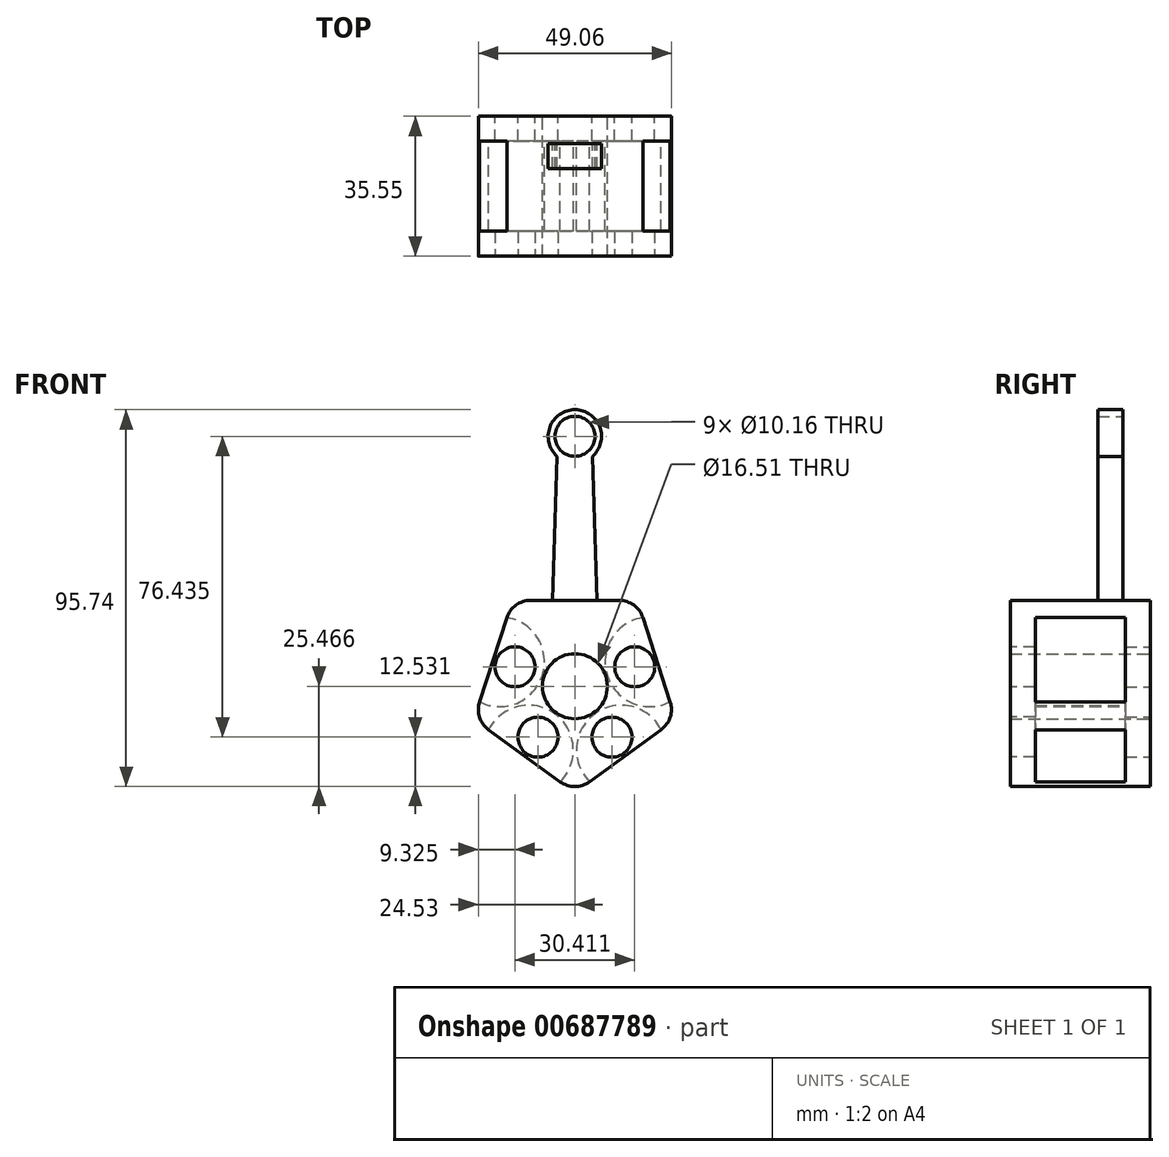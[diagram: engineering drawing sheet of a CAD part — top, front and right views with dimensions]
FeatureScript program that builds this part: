
annotation { "Feature Type Name" : "Feature", "Feature Type Description" : "" }
export const myFeature = defineFeature(function(context is Context, id is Id, definition is map)
    precondition{}
    {
        {
            var Q0;
            Q0=qCreatedBy(makeId("Front.planeOp"),FACE);
            var sketch = newSketch(context, id + "F0", { "sketchPlane" : qUnion([Q0])});
            skPoint(sketch, "E0", {"position": v(-16.39, -3.78) * mm});
            skCircle(sketch, "E1", {"center": v(-16.39, -3.78) * mm, "radius": 8.26 * mm});
            skLineSegment(sketch, "E2.0", {"start": v(-27.63, 18.03) * mm, "end": v(-5.15, 18.03) * mm});
            skLineSegment(sketch, "E2.1", {"start": v(0.89, 13.64) * mm, "end": v(7.83, -7.73) * mm});
            skLineSegment(sketch, "E2.2", {"start": v(5.52, -14.83) * mm, "end": v(-12.66, -28.04) * mm});
            skLineSegment(sketch, "E2.3", {"start": v(-20.12, -28.04) * mm, "end": v(-38.3, -14.83) * mm});
            skLineSegment(sketch, "E2.4", {"start": v(-40.61, -7.73) * mm, "end": v(-33.67, 13.64) * mm});
            skPoint(sketch, "E3", {"position": v(-37.14, 2.96) * mm});
            skPoint(sketch, "E4", {"position": v(-26.76, -0.41) * mm});
            skPoint(sketch, "E5", {"position": v(-31.6, 1.16) * mm});
            skCircle(sketch, "E6", {"center": v(-31.6, 1.16) * mm, "radius": 5.08 * mm});
            skPoint(sketch, "E7", {"position": v(-16.39, 7.12) * mm});
            skPoint(sketch, "E8", {"position": v(4.36, 2.96) * mm});
            skPoint(sketch, "E9", {"position": v(-6.02, -0.41) * mm});
            skPoint(sketch, "E10", {"position": v(-3.57, -21.43) * mm});
            skPoint(sketch, "E11", {"position": v(-29.21, -21.43) * mm});
            skPoint(sketch, "E12", {"position": v(-9.98, -12.6) * mm});
            skPoint(sketch, "E13", {"position": v(-22.8, -12.6) * mm});
            skPoint(sketch, "E14", {"position": v(-1.18, 1.16) * mm});
            skPoint(sketch, "E15", {"position": v(-7, -16.72) * mm});
            skPoint(sketch, "E16", {"position": v(-25.79, -16.72) * mm});
            skCircle(sketch, "E17", {"center": v(-1.18, 1.16) * mm, "radius": 5.08 * mm});
            skCircle(sketch, "E18", {"center": v(-7, -16.72) * mm, "radius": 5.08 * mm});
            skCircle(sketch, "E19", {"center": v(-25.79, -16.72) * mm, "radius": 5.08 * mm});
            skPoint(sketch, "E20.orphan", {"position": v(-36.43, 2.73) * mm});
            skPoint(sketch, "E21.orphan", {"position": v(3.65, 2.73) * mm});
            skPoint(sketch, "E22.end.orphan", {"position": v(-4, -20.83) * mm});
            skPoint(sketch, "E23.end.orphan", {"position": v(-28.77, -20.83) * mm});
            skPoint(sketch, "E24", {"position": v(-24.32, 18.03) * mm});
            skPoint(sketch, "E25", {"position": v(-8.46, 18.03) * mm});
            skPoint(sketch, "E26.visualSharp", {"position": v(-32.24, 18.03) * mm});
            skArc(sketch, "E26.filletArc", {"start": v(-27.63, 18.03) * mm, "mid": v(-31.36, 16.82) * mm, "end": v(-33.67, 13.64) * mm});
            skPoint(sketch, "E27.visualSharp", {"position": v(-0.54, 18.03) * mm});
            skArc(sketch, "E27.filletArc", {"start": v(0.89, 13.64) * mm, "mid": v(-1.42, 16.82) * mm, "end": v(-5.15, 18.03) * mm});
            skPoint(sketch, "E28.visualSharp", {"position": v(9.26, -12.12) * mm});
            skArc(sketch, "E28.filletArc", {"start": v(5.52, -14.83) * mm, "mid": v(7.83, -11.65) * mm, "end": v(7.83, -7.73) * mm});
            skPoint(sketch, "E29.visualSharp", {"position": v(-16.39, -30.75) * mm});
            skArc(sketch, "E29.filletArc", {"start": v(-20.12, -28.04) * mm, "mid": v(-16.39, -29.25) * mm, "end": v(-12.66, -28.04) * mm});
            skPoint(sketch, "E30.visualSharp", {"position": v(-42.04, -12.12) * mm});
            skArc(sketch, "E30.filletArc", {"start": v(-40.61, -7.73) * mm, "mid": v(-40.61, -11.65) * mm, "end": v(-38.3, -14.83) * mm});
            skSolve(sketch);
        }
        {
            var Q0;
            Q0=makeQuery(id+"F0.imprint","IMPRINT",FACE,{"disambiguationData":[TD([[makeQuery(id+"F0.imprint","IMPRINT",EDGE,{"derivedFrom":sQuery(id+"F0.wireOp",EDGE,"E1")}),-1.0]])]});
            extrude(context, id + "F1", {"entities" : qUnion([Q0]), "depth" : 6.35 * mm, "offsetDistance" : 25.4 * mm});
        }
        {
            var Q0;
            Q0=makeQuery(id+"F1.opExtrude","CAP_FACE",FACE,{"disambiguationData":[OSD([sQuery(id+"F0.wireOp",EDGE,"E1"),sQuery(id+"F0.wireOp",EDGE,"E2.0"),sQuery(id+"F0.wireOp",EDGE,"E2.1"),sQuery(id+"F0.wireOp",EDGE,"E2.2"),sQuery(id+"F0.wireOp",EDGE,"E2.3"),sQuery(id+"F0.wireOp",EDGE,"E2.4"),sQuery(id+"F0.wireOp",EDGE,"E6"),sQuery(id+"F0.wireOp",EDGE,"E17"),sQuery(id+"F0.wireOp",EDGE,"E18"),sQuery(id+"F0.wireOp",EDGE,"E19"),sQuery(id+"F0.wireOp",EDGE,"E26.filletArc"),sQuery(id+"F0.wireOp",EDGE,"E27.filletArc"),sQuery(id+"F0.wireOp",EDGE,"E28.filletArc"),sQuery(id+"F0.wireOp",EDGE,"E29.filletArc"),sQuery(id+"F0.wireOp",EDGE,"E30.filletArc")])],"isStart":false});
            var sketch = newSketch(context, id + "F2", { "sketchPlane" : qUnion([Q0])});
            skArc(sketch, "E31", {"start": v(-40.61, -7.73) * mm, "mid": v(-24.66, -1.1) * mm, "end": v(-33.67, 13.64) * mm});
            skArc(sketch, "E32", {"start": v(0.89, 13.64) * mm, "mid": v(-8.15, -1.1) * mm, "end": v(7.83, -7.73) * mm});
            skArc(sketch, "E33", {"start": v(5.52, -14.83) * mm, "mid": v(-11.3, -10.8) * mm, "end": v(-12.66, -28.04) * mm});
            skArc(sketch, "E34", {"start": v(-20.12, -28.04) * mm, "mid": v(-21.48, -10.8) * mm, "end": v(-38.3, -14.83) * mm});
            skSolve(sketch);
        }
        {
            var Q0;
            Q0 = qSketchRegion(id + "F2", true);
            var Q1;
            Q1=makeQuery(id+"F2.imprint","IMPRINT",FACE,{"disambiguationData":[TD([[makeQuery(id+"F2.imprint","IMPRINT",EDGE,{"derivedFrom":sQuery(id+"F2.wireOp",EDGE,"E31")}),-1.0]])]});
            extrude(context, id + "F3", {"entities" : qUnion([Q0, Q1]), "operationType" : NewBodyOperationType.ADD, "depth" : (.75 - (.25 / 2)) * mm, "offsetDistance" : 25.4 * mm});
        }
        {
            var Q0;
            Q0=makeQuery(id+"F3.opExtrude","CAP_FACE",FACE,{"disambiguationData":[OSD([sQuery(id+"F0.wireOp",EDGE,"E1"),sQuery(id+"F0.wireOp",EDGE,"E2.0"),sQuery(id+"F0.wireOp",EDGE,"E26.filletArc"),sQuery(id+"F0.wireOp",EDGE,"E27.filletArc"),sQuery(id+"F0.wireOp",EDGE,"E28.filletArc"),sQuery(id+"F0.wireOp",EDGE,"E29.filletArc"),sQuery(id+"F0.wireOp",EDGE,"E30.filletArc"),sQuery(id+"F2.wireOp",EDGE,"E31"),sQuery(id+"F2.wireOp",EDGE,"E32"),sQuery(id+"F2.wireOp",EDGE,"E33"),sQuery(id+"F2.wireOp",EDGE,"E34")])],"isStart":false});
            var sketch = newSketch(context, id + "F4", { "sketchPlane" : qUnion([Q0])});
            skPoint(sketch, "E35", {"position": v(-16.39, -3.78) * mm});
            skPoint(sketch, "E36", {"position": v(-16.39, 59.72) * mm});
            skCircle(sketch, "E37", {"center": v(-16.39, 59.72) * mm, "radius": 5.08 * mm});
            skCircle(sketch, "E38", {"center": v(-16.39, 59.72) * mm, "radius": 6.77 * mm});
            skPoint(sketch, "E39", {"position": v(-16.39, 54.64) * mm});
            skPoint(sketch, "E40", {"position": v(-11.9, 54.64) * mm});
            skPoint(sketch, "E41", {"position": v(-20.87, 54.64) * mm});
            skPoint(sketch, "E42", {"position": v(-5.15, 18.03) * mm});
            skPoint(sketch, "E43", {"position": v(-27.63, 18.03) * mm});
            skPoint(sketch, "E44", {"position": v(-22.01, 18.03) * mm});
            skPoint(sketch, "E45", {"position": v(-10.77, 18.03) * mm});
            skLineSegment(sketch, "E46", {"start": v(-20.87, 54.64) * mm, "end": v(-22.01, 18.03) * mm});
            skLineSegment(sketch, "E47", {"start": v(-11.9, 54.64) * mm, "end": v(-10.77, 18.03) * mm});
            skSolve(sketch);
        }
        {
            var Q0;
            Q0=makeQuery(id+"F4.imprint","IMPRINT",FACE,{"disambiguationData":[TD([[makeQuery(id+"F4.imprint","IMPRINT",EDGE,{"derivedFrom":makeQuery(id+"F3.opExtrude","CAP_EDGE",EDGE,{"disambiguationData":[OSD([sQuery(id+"F2.wireOp",EDGE,"E31")])],"isStart":false})}),-1.0]])]});
            var Q1;
            {var subQ0=sQuery(id+"F4.wireOp",EDGE,"E46");Q1=makeQuery(id+"F4.imprint","IMPRINT",FACE,{"disambiguationData":[TD([[makeQuery(id+"F4.imprint","IMPRINT",EDGE,{"derivedFrom":subQ0}),1.0]])]});}
            var Q2;
            Q2=makeQuery(id+"F4.imprint","IMPRINT",FACE,{"disambiguationData":[TD([[makeQuery(id+"F4.imprint","IMPRINT",EDGE,{"derivedFrom":sQuery(id+"F4.wireOp",EDGE,"E37")}),-1.0]])]});
            extrude(context, id + "F5", {"entities" : qUnion([Q0, Q1, Q2]), "operationType" : NewBodyOperationType.ADD, "depth" : 6.35 * mm, "offsetDistance" : 25.4 * mm});
        }
        {
            var Q0;
            Q0=makeQuery(id+"F5.opExtrude","CAP_FACE",FACE,{"disambiguationData":[OSD([sQuery(id+"F0.wireOp",EDGE,"E1"),sQuery(id+"F0.wireOp",EDGE,"E2.0"),sQuery(id+"F0.wireOp",EDGE,"E26.filletArc"),sQuery(id+"F0.wireOp",EDGE,"E27.filletArc"),sQuery(id+"F0.wireOp",EDGE,"E28.filletArc"),sQuery(id+"F0.wireOp",EDGE,"E29.filletArc"),sQuery(id+"F0.wireOp",EDGE,"E30.filletArc"),sQuery(id+"F2.wireOp",EDGE,"E31"),sQuery(id+"F2.wireOp",EDGE,"E32"),sQuery(id+"F2.wireOp",EDGE,"E33"),sQuery(id+"F2.wireOp",EDGE,"E34"),sQuery(id+"F4.wireOp",EDGE,"E37"),sQuery(id+"F4.wireOp",EDGE,"E38"),sQuery(id+"F4.wireOp",EDGE,"E46"),sQuery(id+"F4.wireOp",EDGE,"E47")])],"isStart":false});
            var sketch = newSketch(context, id + "F6", { "sketchPlane" : qUnion([Q0])});
            skLineSegment(sketch, "E48", {"start": v(-22.01, 18.03) * mm, "end": v(-10.77, 18.03) * mm});
            skSolve(sketch);
        }
        {
            var Q0;
            Q0 = qSketchRegion(id + "F6", true);
            var Q1;
            Q1=makeQuery(id+"F6.imprint","IMPRINT",FACE,{"disambiguationData":[TD([[makeQuery(id+"F6.imprint","IMPRINT",EDGE,{"derivedFrom":sQuery(id+"F6.wireOp",EDGE,"E48")}),-1.0]])]});
            extrude(context, id + "F7", {"entities" : qUnion([Q0, Q1]), "operationType" : NewBodyOperationType.ADD, "depth" : 15.88 * mm, "offsetDistance" : 25.4 * mm});
        }
        {
            var Q0;
            Q0=makeQuery(id+"F7.opExtrude","CAP_FACE",FACE,{"disambiguationData":[OSD([sQuery(id+"F0.wireOp",EDGE,"E1"),sQuery(id+"F0.wireOp",EDGE,"E2.0"),sQuery(id+"F0.wireOp",EDGE,"E26.filletArc"),sQuery(id+"F0.wireOp",EDGE,"E27.filletArc"),sQuery(id+"F0.wireOp",EDGE,"E28.filletArc"),sQuery(id+"F0.wireOp",EDGE,"E29.filletArc"),sQuery(id+"F0.wireOp",EDGE,"E30.filletArc"),sQuery(id+"F2.wireOp",EDGE,"E31"),sQuery(id+"F2.wireOp",EDGE,"E32"),sQuery(id+"F2.wireOp",EDGE,"E33"),sQuery(id+"F2.wireOp",EDGE,"E34"),sQuery(id+"F6.wireOp",EDGE,"E48")])],"isStart":false});
            var sketch = newSketch(context, id + "F8", { "sketchPlane" : qUnion([Q0])});
            skLineSegment(sketch, "E49", {"start": v(-27.63, 18.03) * mm, "end": v(-5.15, 18.03) * mm});
            skLineSegment(sketch, "E50", {"start": v(-33.67, 13.64) * mm, "end": v(-40.61, -7.73) * mm});
            skLineSegment(sketch, "E51", {"start": v(-38.3, -14.83) * mm, "end": v(-20.12, -28.04) * mm});
            skLineSegment(sketch, "E52", {"start": v(-12.66, -28.04) * mm, "end": v(5.52, -14.83) * mm});
            skLineSegment(sketch, "E53", {"start": v(7.83, -7.73) * mm, "end": v(0.89, 13.64) * mm});
            skArc(sketch, "E54", {"start": v(-27.63, 18.03) * mm, "mid": v(-31.36, 16.82) * mm, "end": v(-33.67, 13.64) * mm});
            skArc(sketch, "E55", {"start": v(0.89, 13.64) * mm, "mid": v(-1.42, 16.82) * mm, "end": v(-5.15, 18.03) * mm});
            skArc(sketch, "E56", {"start": v(6.04, -14.41) * mm, "mid": v(7.93, -11.34) * mm, "end": v(7.83, -7.73) * mm});
            skArc(sketch, "E57", {"start": v(-20.12, -28.04) * mm, "mid": v(-16.39, -29.25) * mm, "end": v(-12.66, -28.04) * mm});
            skArc(sketch, "E58", {"start": v(-40.61, -7.73) * mm, "mid": v(-40.61, -11.65) * mm, "end": v(-38.3, -14.83) * mm});
            skPoint(sketch, "E59", {"position": v(-37.14, 2.96) * mm});
            skSolve(sketch);
        }
        {
            var Q0;
            Q0=makeQuery(id+"F8.imprint","IMPRINT",FACE,{"disambiguationData":[TD([[makeQuery(id+"F8.imprint","IMPRINT",EDGE,{"derivedFrom":sQuery(id+"F8.wireOp",EDGE,"E49")}),-1.0]])]});
            var Q1;
            Q1=makeQuery(id+"F8.imprint","IMPRINT",FACE,{"disambiguationData":[TD([[makeQuery(id+"F8.imprint","IMPRINT",EDGE,{"derivedFrom":sQuery(id+"F8.wireOp",EDGE,"E53")}),1.0]])]});
            var Q2;
            Q2=makeQuery(id+"F8.imprint","IMPRINT",FACE,{"disambiguationData":[TD([[makeQuery(id+"F8.imprint","IMPRINT",EDGE,{"derivedFrom":sQuery(id+"F8.wireOp",EDGE,"E50")}),1.0]])]});
            var Q3;
            Q3=makeQuery(id+"F8.imprint","IMPRINT",FACE,{"disambiguationData":[TD([[makeQuery(id+"F8.imprint","IMPRINT",EDGE,{"derivedFrom":sQuery(id+"F8.wireOp",EDGE,"E51")}),1.0]])]});
            var Q4;
            Q4=makeQuery(id+"F8.imprint","IMPRINT",FACE,{"disambiguationData":[TD([[makeQuery(id+"F8.imprint","IMPRINT",EDGE,{"derivedFrom":sQuery(id+"F8.wireOp",EDGE,"E52")}),1.0]])]});
            extrude(context, id + "F9", {"entities" : qUnion([Q0, Q1, Q2, Q3, Q4]), "operationType" : NewBodyOperationType.ADD, "depth" : 6.35 * mm, "offsetDistance" : 25.4 * mm});
        }
        {
            var Q0;
            Q0=makeQuery(id+"F9.opExtrude","CAP_FACE",FACE,{"disambiguationData":[OSD([sQuery(id+"F0.wireOp",EDGE,"E1"),sQuery(id+"F0.wireOp",EDGE,"E28.filletArc"),sQuery(id+"F8.wireOp",EDGE,"E49"),sQuery(id+"F8.wireOp",EDGE,"E50"),sQuery(id+"F8.wireOp",EDGE,"E51"),sQuery(id+"F8.wireOp",EDGE,"E52"),sQuery(id+"F8.wireOp",EDGE,"E53"),sQuery(id+"F8.wireOp",EDGE,"E54"),sQuery(id+"F8.wireOp",EDGE,"E55"),sQuery(id+"F8.wireOp",EDGE,"E56"),sQuery(id+"F8.wireOp",EDGE,"E57"),sQuery(id+"F8.wireOp",EDGE,"E58")])],"isStart":false});
            var sketch = newSketch(context, id + "F10", { "sketchPlane" : qUnion([Q0])});
            skPoint(sketch, "E60", {"position": v(4.36, 2.96) * mm});
            skPoint(sketch, "E61", {"position": v(-3.57, -21.43) * mm});
            skPoint(sketch, "E62", {"position": v(-29.21, -21.43) * mm});
            skPoint(sketch, "E63", {"position": v(-37.14, 2.96) * mm});
            skPoint(sketch, "E64", {"position": v(-16.39, -3.78) * mm});
            skLineSegment(sketch, "E65", {"start": v(-29.21, -21.43) * mm, "end": v(-22.8, -12.62) * mm});
            skLineSegment(sketch, "E66", {"start": v(-3.57, -21.43) * mm, "end": v(-9.97, -12.62) * mm});
            skLineSegment(sketch, "E67", {"start": v(4.36, 2.96) * mm, "end": v(-6, -0.4) * mm});
            skLineSegment(sketch, "E68", {"start": v(-37.14, 2.96) * mm, "end": v(-26.78, -0.4) * mm});
            skPoint(sketch, "E69", {"position": v(-31.6, 1.16) * mm});
            skPoint(sketch, "E70", {"position": v(-1.18, 1.16) * mm});
            skPoint(sketch, "E71", {"position": v(-7, -16.72) * mm});
            skPoint(sketch, "E72", {"position": v(-25.79, -16.72) * mm});
            skCircle(sketch, "E73", {"center": v(-31.6, 1.16) * mm, "radius": 5.08 * mm});
            skCircle(sketch, "E74", {"center": v(-25.79, -16.72) * mm, "radius": 5.08 * mm});
            skCircle(sketch, "E75", {"center": v(-7, -16.72) * mm, "radius": 5.08 * mm});
            skCircle(sketch, "E76", {"center": v(-1.18, 1.16) * mm, "radius": 5.08 * mm});
            skSolve(sketch);
        }
        {
            var Q0;
            Q0=makeQuery(id+"F10.imprint","IMPRINT",FACE,{"disambiguationData":[TD([[makeQuery(id+"F10.imprint","IMPRINT",EDGE,{"derivedFrom":sQuery(id+"F10.wireOp",EDGE,"E76")}),1.0]])]});
            var Q1;
            Q1=makeQuery(id+"F10.imprint","IMPRINT",FACE,{"disambiguationData":[TD([[makeQuery(id+"F10.imprint","IMPRINT",EDGE,{"derivedFrom":sQuery(id+"F10.wireOp",EDGE,"E75")}),1.0]])]});
            var Q2;
            Q2=makeQuery(id+"F10.imprint","IMPRINT",FACE,{"disambiguationData":[TD([[makeQuery(id+"F10.imprint","IMPRINT",EDGE,{"derivedFrom":sQuery(id+"F10.wireOp",EDGE,"E74")}),1.0]])]});
            var Q3;
            Q3=makeQuery(id+"F10.imprint","IMPRINT",FACE,{"disambiguationData":[TD([[makeQuery(id+"F10.imprint","IMPRINT",EDGE,{"derivedFrom":sQuery(id+"F10.wireOp",EDGE,"E73")}),1.0]])]});
            extrude(context, id + "F11", {"entities" : qUnion([Q0, Q1, Q2, Q3]), "operationType" : NewBodyOperationType.REMOVE, "oppositeDirection" : true, "depth" : 25.4 * mm, "offsetDistance" : 25.4 * mm});
        }
    });
